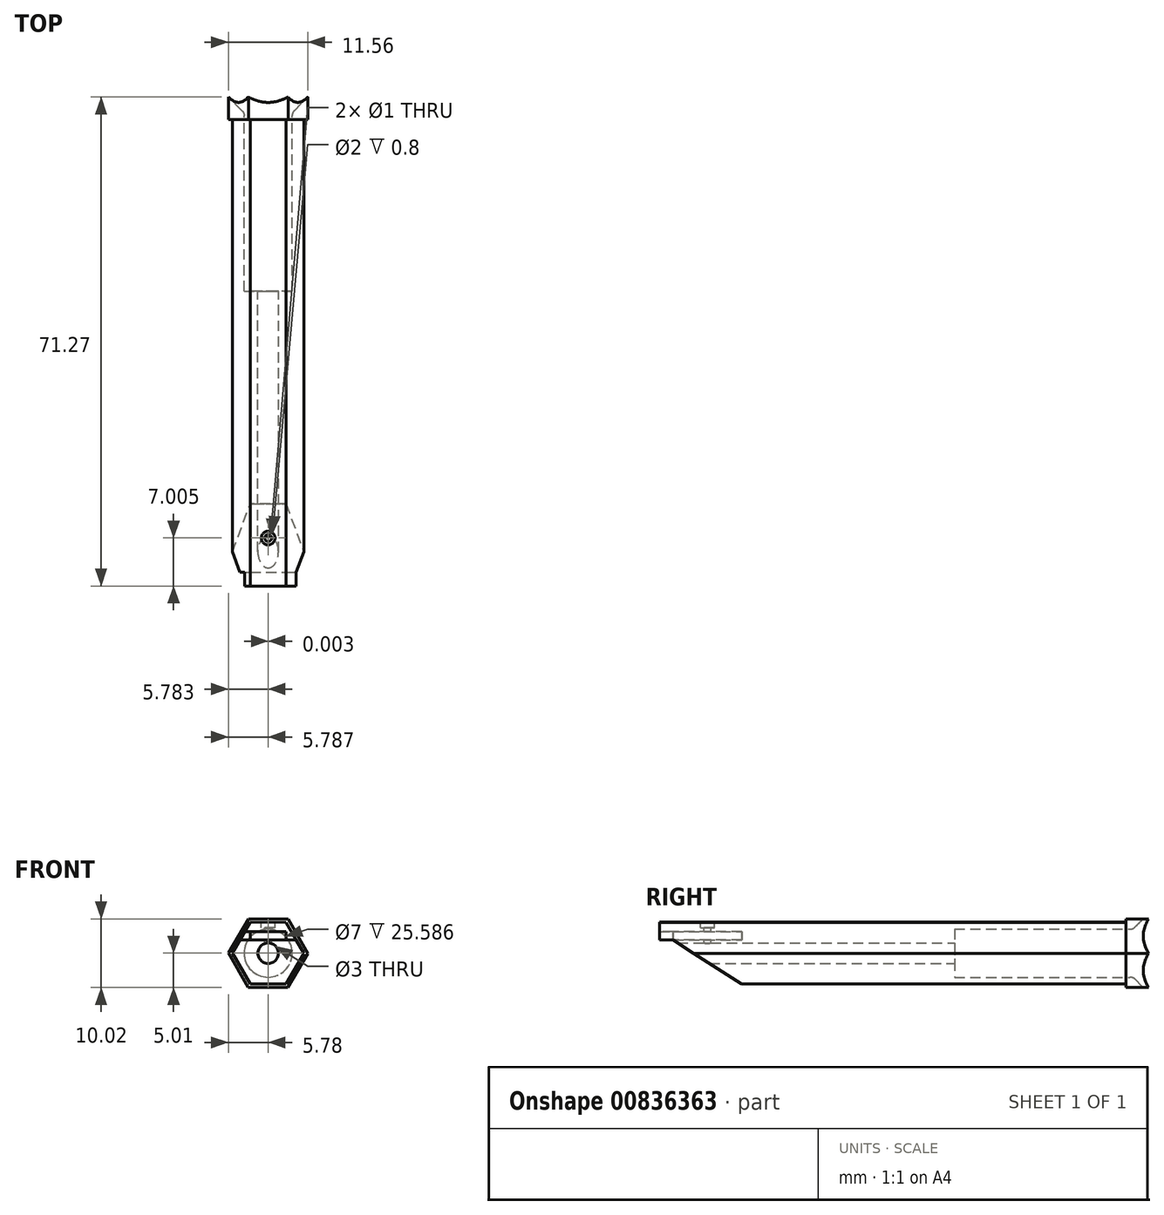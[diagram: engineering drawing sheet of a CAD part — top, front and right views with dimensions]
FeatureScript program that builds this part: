
annotation { "Feature Type Name" : "Feature", "Feature Type Description" : "" }
export const myFeature = defineFeature(function(context is Context, id is Id, definition is map)
    precondition{}
    {
        {
            var Q0;
            Q0=qCreatedBy(makeId("Front.planeOp"),FACE);
            var sketch = newSketch(context, id + "F0", { "sketchPlane" : qUnion([Q0])});
            skLineSegment(sketch, "E0.0", {"start": v(2.6, 4.5) * mm, "end": v(5.2, 0) * mm});
            skLineSegment(sketch, "E0.1", {"start": v(5.2, 0) * mm, "end": v(2.6, -4.5) * mm});
            skLineSegment(sketch, "E0.2", {"start": v(2.6, -4.5) * mm, "end": v(-2.6, -4.5) * mm});
            skLineSegment(sketch, "E0.3", {"start": v(-2.6, -4.5) * mm, "end": v(-5.2, 0) * mm});
            skLineSegment(sketch, "E0.4", {"start": v(-5.2, 0) * mm, "end": v(-2.6, 4.5) * mm});
            skLineSegment(sketch, "E0.5", {"start": v(-2.6, 4.5) * mm, "end": v(2.6, 4.5) * mm});
            skPoint(sketch, "E0.0.midPoint", {"position": v(3.9, 2.25) * mm});
            skSolve(sketch);
        }
        {
            var Q0;
            Q0=makeQuery(id+"F0.imprint","IMPRINT",FACE,{"disambiguationData":[TD([[makeQuery(id+"F0.imprint","IMPRINT",EDGE,{"derivedFrom":sQuery(id+"F0.wireOp",EDGE,"E0.0")}),-1.0]])]});
            extrude(context, id + "F1", {"entities" : qUnion([Q0]), "depth" : 70 * mm, "offsetDistance" : 25 * mm});
        }
        {
            var Q0;
            Q0=makeQuery(id+"F1.opExtrude","CAP_FACE",FACE,{"disambiguationData":[OSD([sQuery(id+"F0.wireOp",EDGE,"E0.0"),sQuery(id+"F0.wireOp",EDGE,"E0.1"),sQuery(id+"F0.wireOp",EDGE,"E0.2"),sQuery(id+"F0.wireOp",EDGE,"E0.3"),sQuery(id+"F0.wireOp",EDGE,"E0.4"),sQuery(id+"F0.wireOp",EDGE,"E0.5")])],"isStart":true});
            var sketch = newSketch(context, id + "F2", { "sketchPlane" : qUnion([Q0])});
            skLineSegment(sketch, "E1", {"start": v(2.6, 4.5) * mm, "end": v(5.2, 0) * mm});
            skLineSegment(sketch, "E2", {"start": v(5.2, 0) * mm, "end": v(3.9, 2.26) * mm});
            skSolve(sketch);
        }
        {
            var Q0;
            Q0=makeQuery(id+"F2.imprint","IMPRINT",FACE,{"disambiguationData":[TD([[makeQuery(id+"F2.imprint","IMPRINT",EDGE,{"derivedFrom":sQuery(id+"F2.wireOp",EDGE,"E1")}),1.0]])]});
            var sketch = newSketch(context, id + "F3", { "sketchPlane" : qUnion([Q0])});
            skLineSegment(sketch, "E3.1", {"start": v(5.86, 0.15) * mm, "end": v(2.73, -5.28) * mm});
            skLineSegment(sketch, "E3.5", {"start": v(-3.06, 5) * mm, "end": v(3.2, 5) * mm});
            skPoint(sketch, "E3.0.midPoint", {"position": v(4.74, 2.65) * mm});
            skLineSegment(sketch, "E4", {"start": v(-5.2, 0) * mm, "end": v(-2.6, -4.5) * mm});
            skLineSegment(sketch, "E5", {"start": v(-2.6, -4.5) * mm, "end": v(2.6, -4.5) * mm});
            skLineSegment(sketch, "E6", {"start": v(2.6, -4.5) * mm, "end": v(5.2, 0) * mm});
            skLineSegment(sketch, "E7", {"start": v(5.2, 0) * mm, "end": v(2.6, 4.5) * mm});
            skLineSegment(sketch, "E8", {"start": v(2.6, 4.5) * mm, "end": v(-2.6, 4.5) * mm});
            skLineSegment(sketch, "E9", {"start": v(-2.6, 4.5) * mm, "end": v(-5.2, 0) * mm});
            skLineSegment(sketch, "E10", {"start": v(2.16, 4.5) * mm, "end": v(2.16, 5) * mm});
            skLineSegment(sketch, "E11", {"start": v(-2.12, 4.5) * mm, "end": v(-2.12, 5) * mm});
            skLineSegment(sketch, "E12", {"start": v(-2.85, 4.07) * mm, "end": v(-3.29, 4.32) * mm});
            skLineSegment(sketch, "E13", {"start": v(-4.92, 0.48) * mm, "end": v(-5.35, 0.73) * mm});
            skLineSegment(sketch, "E14", {"start": v(-4.8, -0.7) * mm, "end": v(-5.24, -0.95) * mm});
            skLineSegment(sketch, "E15", {"start": v(-2.97, -3.86) * mm, "end": v(-3.4, -4.1) * mm});
            skLineSegment(sketch, "E16", {"start": v(-2.19, -4.5) * mm, "end": v(-2.19, -5) * mm});
            skLineSegment(sketch, "E17", {"start": v(2.17, -4.5) * mm, "end": v(2.17, -5) * mm});
            skLineSegment(sketch, "E18", {"start": v(2.9, -3.98) * mm, "end": v(3.34, -4.23) * mm});
            skLineSegment(sketch, "E19", {"start": v(4.97, -0.38) * mm, "end": v(5.4, -0.63) * mm});
            skLineSegment(sketch, "E20", {"start": v(4.86, 0.59) * mm, "end": v(5.3, 0.84) * mm});
            skLineSegment(sketch, "E21", {"start": v(2.88, 4.02) * mm, "end": v(3.3, 4.27) * mm});
            skLineSegment(sketch, "E22", {"start": v(3.3, 4.27) * mm, "end": v(5.78, 0) * mm});
            skLineSegment(sketch, "E23", {"start": v(3.3, 4.27) * mm, "end": v(2.88, 5) * mm});
            skLineSegment(sketch, "E24", {"start": v(-5.35, 0.73) * mm, "end": v(-2.9, 5) * mm});
            skLineSegment(sketch, "E25", {"start": v(-2.19, -5) * mm, "end": v(2.9, -5) * mm});
            skLineSegment(sketch, "E26", {"start": v(-2.19, -5) * mm, "end": v(-2.88, -5) * mm});
            skLineSegment(sketch, "E27", {"start": v(-5.24, -0.95) * mm, "end": v(-2.77, -5.2) * mm});
            skLineSegment(sketch, "E28", {"start": v(-3.29, 4.32) * mm, "end": v(-6.02, -0.44) * mm});
            skLineSegment(sketch, "E29", {"start": v(-5.24, -0.95) * mm, "end": v(-5.78, 0) * mm});
            skSolve(sketch);
        }
        {
            var Q0;
            Q0=makeQuery(id+"F2.imprint","IMPRINT",FACE,{"disambiguationData":[TD([[makeQuery(id+"F2.imprint","IMPRINT",EDGE,{"derivedFrom":sQuery(id+"F2.wireOp",EDGE,"E1")}),1.0]])]});
            var sketch = newSketch(context, id + "F4", { "sketchPlane" : qUnion([Q0])});
            skCircle(sketch, "E30", {"center": v(0, 0) * mm, "radius": 3.5 * mm});
            skSolve(sketch);
        }
        {
            var Q0;
            Q0=qSketchRegion(id+"F4",true);
            extrude(context, id + "F5", {"entities" : qUnion([Q0]), "operationType" : NewBodyOperationType.REMOVE, "oppositeDirection" : true, "depth" : 25 * mm, "offsetDistance" : 25 * mm});
        }
        {
            var Q0;
            Q0=makeQuery(id+"F1.opExtrude","SWEPT_FACE",FACE,{"disambiguationData":[OSD([sQuery(id+"F0.wireOp",EDGE,"E0.0")])]});
            var sketch = newSketch(context, id + "F6", { "sketchPlane" : qUnion([Q0])});
            skLineSegment(sketch, "E31", {"start": v(-70, 2.6) * mm, "end": v(-70, -2.6) * mm});
            skLineSegment(sketch, "E32", {"start": v(-70, -2.6) * mm, "end": v(-63, -2.6) * mm});
            skLineSegment(sketch, "E33", {"start": v(-63, -2.6) * mm, "end": v(-70, 2.6) * mm});
            skSolve(sketch);
        }
        {
            var Q0;
            Q0=makeQuery(id+"F1.opExtrude","SWEPT_FACE",FACE,{"disambiguationData":[OSD([sQuery(id+"F0.wireOp",EDGE,"E0.4")])]});
            var sketch = newSketch(context, id + "F7", { "sketchPlane" : qUnion([Q0])});
            skLineSegment(sketch, "E34", {"start": v(70, 2.6) * mm, "end": v(70, -2.6) * mm});
            skLineSegment(sketch, "E35", {"start": v(70, -2.6) * mm, "end": v(63, -2.6) * mm});
            skLineSegment(sketch, "E36", {"start": v(63, -2.6) * mm, "end": v(70, 2.6) * mm});
            skSolve(sketch);
        }
        {
            var Q0;
            Q0=qSketchRegion(id+"F6",true);
            extrude(context, id + "F8", {"entities" : qUnion([Q0]), "operationType" : NewBodyOperationType.REMOVE, "oppositeDirection" : true, "depth" : 25 * mm, "offsetDistance" : 25 * mm, "hasDraft" : true, "draftAngle" : 24.87 * degree});
        }
        {
            var Q0;
            Q0=makeQuery(id+"F7.imprint","IMPRINT",FACE,{"disambiguationData":[TD([[makeQuery(id+"F7.imprint","IMPRINT",EDGE,{"derivedFrom":sQuery(id+"F7.wireOp",EDGE,"E34")}),1.0]])]});
            extrude(context, id + "F9", {"entities" : qUnion([Q0]), "operationType" : NewBodyOperationType.REMOVE, "oppositeDirection" : true, "depth" : 25 * mm, "offsetDistance" : 25 * mm, "hasDraft" : true, "draftAngle" : 24.87 * degree});
        }
        {
            var Q0;
            Q0=makeQuery(id+"F1.opExtrude","SWEPT_FACE",FACE,{"disambiguationData":[OSD([sQuery(id+"F0.wireOp",EDGE,"E0.0")])]});
            var sketch = newSketch(context, id + "F10", { "sketchPlane" : qUnion([Q0])});
            skLineSegment(sketch, "E37", {"start": v(-68.6, 2.16) * mm, "end": v(-68.6, 2.6) * mm});
            skLineSegment(sketch, "E38", {"start": v(-65.98, 2.6) * mm, "end": v(-65.98, -0.38) * mm});
            skLineSegment(sketch, "E39", {"start": v(-65.98, -0.38) * mm, "end": v(-65.98, 1.1) * mm});
            skPoint(sketch, "E40", {"position": v(-65.98, 1.1) * mm});
            skLineSegment(sketch, "E41", {"start": v(-65.98, 2.6) * mm, "end": v(-70, 2.6) * mm});
            skSolve(sketch);
        }
        {
            var Q0;
            Q0=makeQuery(id+"F1.opExtrude","SWEPT_FACE",FACE,{"disambiguationData":[OSD([sQuery(id+"F0.wireOp",EDGE,"E0.4")])]});
            var sketch = newSketch(context, id + "F11", { "sketchPlane" : qUnion([Q0])});
            skLineSegment(sketch, "E42", {"start": v(70, 2.6) * mm, "end": v(65.99, 2.6) * mm});
            skLineSegment(sketch, "E43", {"start": v(65.99, 2.6) * mm, "end": v(65.99, -0.38) * mm});
            skLineSegment(sketch, "E44", {"start": v(65.99, -0.38) * mm, "end": v(70, 2.6) * mm});
            skLineSegment(sketch, "E45", {"start": v(65.99, 2.6) * mm, "end": v(65.99, 1.1) * mm});
            skPoint(sketch, "E46", {"position": v(65.99, 1.1) * mm});
            skSolve(sketch);
        }
        {
            var Q0;
            Q0=makeQuery(id+"F1.opExtrude","SWEPT_FACE",FACE,{"disambiguationData":[OSD([sQuery(id+"F0.wireOp",EDGE,"E0.5")])]});
            var sketch = newSketch(context, id + "F12", { "sketchPlane" : qUnion([Q0])});
            skLineSegment(sketch, "E47", {"start": v(-2.6, -70) * mm, "end": v(-2.6, -65.98) * mm});
            skLineSegment(sketch, "E48", {"start": v(-2.6, -65.98) * mm, "end": v(2.6, -65.98) * mm});
            skLineSegment(sketch, "E49", {"start": v(2.6, -65.98) * mm, "end": v(2.6, -70) * mm});
            skLineSegment(sketch, "E50", {"start": v(2.6, -70) * mm, "end": v(-2.6, -70) * mm});
            skSolve(sketch);
        }
        {
            var Q0;
            Q0=qSketchRegion(id+"F12",true);
            extrude(context, id + "F13", {"entities" : qUnion([Q0]), "operationType" : NewBodyOperationType.REMOVE, "oppositeDirection" : true, "depth" : 25 * mm, "offsetDistance" : 25 * mm});
        }
        {
            var Q0;
            Q0=makeQuery(id+"F11.imprint","IMPRINT",FACE,{"disambiguationData":[TD([[makeQuery(id+"F11.imprint","IMPRINT",EDGE,{"derivedFrom":sQuery(id+"F11.wireOp",EDGE,"E42")}),1.0]])]});
            extrude(context, id + "F14", {"entities" : qUnion([Q0]), "operationType" : NewBodyOperationType.REMOVE, "oppositeDirection" : true, "depth" : 25 * mm, "offsetDistance" : 25 * mm});
        }
        {
            var Q0;
            {var subQ4=sQuery(id+"F10.wireOp",EDGE,"E38");Q0=makeQuery(id+"F10.imprint","IMPRINT",FACE,{"disambiguationData":[TD([[makeQuery(id+"F10.imprint","IMPRINT",EDGE,{"derivedFrom":subQ4}),-1.0]])]});}
            extrude(context, id + "F15", {"entities" : qUnion([Q0]), "operationType" : NewBodyOperationType.REMOVE, "oppositeDirection" : true, "depth" : 25 * mm, "offsetDistance" : 25 * mm});
        }
        {
            var Q0;
            Q0=makeQuery(id+"F14.boolean.opBoolean","MERGE",FACE,{"derivedFrom":[makeQuery(id+"F13.boolean.opBoolean","COPY",FACE,{"derivedFrom":makeQuery(id+"F13.opExtrude","SWEPT_FACE",FACE,{"disambiguationData":[OSD([sQuery(id+"F12.wireOp",EDGE,"E48")])]})}),makeQuery(id+"F14.opExtrude","SWEPT_FACE",FACE,{"disambiguationData":[OSD([sQuery(id+"F11.wireOp",EDGE,"E43"),sQuery(id+"F11.wireOp",EDGE,"E45")])]})]});
            var sketch = newSketch(context, id + "F16", { "sketchPlane" : qUnion([Q0])});
            skLineSegment(sketch, "E51", {"start": v(-2.6, 4.5) * mm, "end": v(-2.6, 4.5) * mm});
            skLineSegment(sketch, "E52", {"start": v(-2.6, 4.5) * mm, "end": v(-2.6, 2.5) * mm});
            skLineSegment(sketch, "E53", {"start": v(2.6, 4.5) * mm, "end": v(2.6, 4.5) * mm});
            skLineSegment(sketch, "E54", {"start": v(2.6, 4.5) * mm, "end": v(2.2, -231.47) * mm});
            skLineSegment(sketch, "E55", {"start": v(-2.6, 2.5) * mm, "end": v(-2.6, 3.7) * mm});
            skLineSegment(sketch, "E56", {"start": v(2.2, -231.47) * mm, "end": v(2.4, -113.49) * mm});
            skLineSegment(sketch, "E57", {"start": v(2.2, -231.47) * mm, "end": v(3, 237.7) * mm});
            skLineSegment(sketch, "E58", {"start": v(-2.6, 2.5) * mm, "end": v(-2.6, 1.93) * mm});
            skLineSegment(sketch, "E59", {"start": v(2.2, 1.92) * mm, "end": v(2.2, -231.47) * mm});
            skLineSegment(sketch, "E60", {"start": v(2.2, 1.92) * mm, "end": v(-2.6, 1.93) * mm});
            skLineSegment(sketch, "E61", {"start": v(-2.6, 1.93) * mm, "end": v(-2.6, 3.13) * mm});
            skLineSegment(sketch, "E62", {"start": v(2.6, 3.12) * mm, "end": v(-2.6, 3.13) * mm});
            skLineSegment(sketch, "E63", {"start": v(2.6, 4.5) * mm, "end": v(2.6, 1.92) * mm});
            skLineSegment(sketch, "E64", {"start": v(2.6, 1.92) * mm, "end": v(2.6, 3.12) * mm});
            skSolve(sketch);
        }
        {
            var Q0;
            {var subQ1=sQuery(id+"F16.wireOp",EDGE,"E60");Q0=makeQuery(id+"F16.imprint","IMPRINT",FACE,{"disambiguationData":[TD([[makeQuery(id+"F16.imprint","IMPRINT",EDGE,{"derivedFrom":subQ1}),1.0]])]});}
            extrude(context, id + "F17", {"entities" : qUnion([Q0]), "operationType" : NewBodyOperationType.REMOVE, "oppositeDirection" : true, "depth" : 10 * mm, "offsetDistance" : 25 * mm});
        }
        {
            var Q0;
            Q0=makeQuery(id+"F1.opExtrude","SWEPT_FACE",FACE,{"disambiguationData":[OSD([sQuery(id+"F0.wireOp",EDGE,"E0.5")])]});
            var sketch = newSketch(context, id + "F18", { "sketchPlane" : qUnion([Q0])});
            skLineSegment(sketch, "E65", {"start": v(-2.6, -65.98) * mm, "end": v(2.6, -65.98) * mm});
            skLineSegment(sketch, "E66", {"start": v(2.6, -65.98) * mm, "end": v(2.6, -55.98) * mm});
            skLineSegment(sketch, "E67", {"start": v(2.6, -55.98) * mm, "end": v(-2.6, -55.98) * mm});
            skLineSegment(sketch, "E68", {"start": v(-2.6, -55.98) * mm, "end": v(-2.6, -65.98) * mm});
            skLineSegment(sketch, "E69", {"start": v(-2.6, -60.98) * mm, "end": v(2.6, -60.98) * mm});
            skLineSegment(sketch, "E70", {"start": v(2.6, -60.98) * mm, "end": v(0, -60.98) * mm});
            skLineSegment(sketch, "E71", {"start": v(0, -60.98) * mm, "end": v(0, -55.98) * mm});
            skLineSegment(sketch, "E72", {"start": v(0, -55.98) * mm, "end": v(0, -65.98) * mm});
            skPoint(sketch, "E73", {"position": v(0, -60.98) * mm});
            skSolve(sketch);
        }
        {
            var Q0;
            Q0=sQuery(id+"F18.wireOp",VERTEX,"E73");
            var Q1;
            Q1=makeQuery(id+"F1.opExtrude","SWEPT_BODY",BODY,{"disambiguationData":[OSD([sQuery(id+"F0.wireOp",EDGE,"E0.0"),sQuery(id+"F0.wireOp",EDGE,"E0.1"),sQuery(id+"F0.wireOp",EDGE,"E0.2"),sQuery(id+"F0.wireOp",EDGE,"E0.3"),sQuery(id+"F0.wireOp",EDGE,"E0.4"),sQuery(id+"F0.wireOp",EDGE,"E0.5")])]});
            hole(context, id + "F19", {"style" : HoleStyle.C_BORE, "endStyle" : HoleEndStyle.BLIND, "holeDiameter" : 1 * mm, "cBoreDiameter" : 2 * mm, "cBoreDepth" : .8 * mm, "majorDiameter" : 5 * mm, "holeDepth" : 2 * mm, "isTappedThrough" : true, "tappedDepth" : 12 * mm, "tapClearance" : 3, "startFromSketch" : true, "locations" : qUnion([Q0]), "scope" : qUnion([Q1])});
        }
        {
            var Q0;
            Q0=makeQuery(id+"F17.boolean.opBoolean","COPY",FACE,{"derivedFrom":makeQuery(id+"F17.opExtrude","SWEPT_FACE",FACE,{"disambiguationData":[OSD([sQuery(id+"F6.wireOp",EDGE,"E33"),sQuery(id+"F12.wireOp",EDGE,"E48"),sQuery(id+"F16.wireOp",EDGE,"E60")])]})});
            var sketch = newSketch(context, id + "F20", { "sketchPlane" : qUnion([Q0])});
            skLineSegment(sketch, "E74", {"start": v(-2.6, -65.99) * mm, "end": v(-2.6, -55.99) * mm});
            skLineSegment(sketch, "E75", {"start": v(-2.6, -55.99) * mm, "end": v(2.6, -55.98) * mm});
            skLineSegment(sketch, "E76", {"start": v(2.6, -55.98) * mm, "end": v(2.6, -65.98) * mm});
            skLineSegment(sketch, "E77", {"start": v(2.6, -65.98) * mm, "end": v(-2.6, -65.99) * mm});
            skLineSegment(sketch, "E78", {"start": v(0, -65.98) * mm, "end": v(0, -55.98) * mm});
            skLineSegment(sketch, "E79", {"start": v(2.6, -60.98) * mm, "end": v(-2.6, -60.99) * mm});
            skPoint(sketch, "E80", {"position": v(0, -60.98) * mm});
            skSolve(sketch);
        }
        {
            var Q0;
            Q0=sQuery(id+"F20.wireOp",VERTEX,"E80");
            var Q1;
            Q1=makeQuery(id+"F1.opExtrude","SWEPT_BODY",BODY,{"disambiguationData":[OSD([sQuery(id+"F0.wireOp",EDGE,"E0.0"),sQuery(id+"F0.wireOp",EDGE,"E0.1"),sQuery(id+"F0.wireOp",EDGE,"E0.2"),sQuery(id+"F0.wireOp",EDGE,"E0.3"),sQuery(id+"F0.wireOp",EDGE,"E0.4"),sQuery(id+"F0.wireOp",EDGE,"E0.5")])]});
            hole(context, id + "F21", {"style" : HoleStyle.SIMPLE, "endStyle" : HoleEndStyle.BLIND, "holeDiameter" : 1 * mm, "majorDiameter" : 5 * mm, "holeDepth" : 2 * mm, "isTappedThrough" : true, "tappedDepth" : 12 * mm, "tapClearance" : 3, "startFromSketch" : true, "locations" : qUnion([Q0]), "scope" : qUnion([Q1])});
        }
        {
            var Q0;
            Q0=makeQuery(id+"F5.boolean.opBoolean","COPY",FACE,{"derivedFrom":makeQuery(id+"F5.opExtrude","CAP_FACE",FACE,{"disambiguationData":[OSD([sQuery(id+"F4.wireOp",EDGE,"E30")])],"isStart":false})});
            var sketch = newSketch(context, id + "F22", { "sketchPlane" : qUnion([Q0])});
            skCircle(sketch, "E81", {"center": v(0, 0) * mm, "radius": 1.5 * mm});
            skSolve(sketch);
        }
        {
            var Q0;
            {var subQ2=makeQuery(id+"F2.imprint","IMPRINT",EDGE,{"derivedFrom":sQuery(id+"F2.wireOp",EDGE,"E1")});Q0=makeQuery(id+"F3.imprint","IMPRINT",FACE,{"disambiguationData":[TD([[makeQuery(id+"F3.imprint","IMPRINT",EDGE,{"derivedFrom":subQ2}),1.0]])]});}
            var sketch = newSketch(context, id + "F23", { "sketchPlane" : qUnion([Q0])});
            skCircle(sketch, "E82", {"center": v(0, 0) * mm, "radius": 3.5 * mm});
            skSolve(sketch);
        }
        {
            var Q0;
            Q0=makeQuery(id+"F23.imprint","IMPRINT",FACE,{"disambiguationData":[TD([[makeQuery(id+"F23.imprint","IMPRINT",EDGE,{"derivedFrom":sQuery(id+"F23.wireOp",EDGE,"E82")}),-1.0]])]});
            extrude(context, id + "F24", {"entities" : qUnion([Q0]), "operationType" : NewBodyOperationType.ADD, "depth" : 5 * mm, "offsetDistance" : 25 * mm});
        }
        {
            var Q0;
            Q0=qSketchRegion(id+"F3",true);
            extrude(context, id + "F25", {"entities" : qUnion([Q0]), "operationType" : NewBodyOperationType.ADD, "depth" : 5 * mm, "offsetDistance" : 25 * mm});
        }
        {
            var Q0;
            Q0=makeQuery(id+"F24.opExtrude","CAP_EDGE",EDGE,{"disambiguationData":[OSD([sQuery(id+"F23.wireOp",EDGE,"E82")])],"isStart":false});
            chamfer(context, id + "F26", {"entities" : qUnion([Q0]), "width" : 4 * mm, "tangentPropagation" : true});
        }
        {
            var Q0;
            {var subQ0=sQuery(id+"F23.wireOp",EDGE,"E82");Q0=makeQuery(id+"F26.opChamfer","BLEND_EDGE",EDGE,{"blendedFrom":[makeQuery(id+"F24.opExtrude","CAP_EDGE",EDGE,{"disambiguationData":[OSD([subQ0])],"isStart":false}),makeQuery(id+"F24.boolean.opBoolean","MERGE",FACE,{"derivedFrom":[makeQuery(id+"F5.boolean.opBoolean","COPY",FACE,{"derivedFrom":makeQuery(id+"F5.opExtrude","SWEPT_FACE",FACE,{"disambiguationData":[OSD([sQuery(id+"F4.wireOp",EDGE,"E30")])]})}),makeQuery(id+"F24.opExtrude","SWEPT_FACE",FACE,{"disambiguationData":[OSD([subQ0])]})]})],"blendedInto":[makeQuery(id+"F24.boolean.opBoolean","MERGE",FACE,{"derivedFrom":[makeQuery(id+"F5.boolean.opBoolean","COPY",FACE,{"derivedFrom":makeQuery(id+"F5.opExtrude","SWEPT_FACE",FACE,{"disambiguationData":[OSD([sQuery(id+"F4.wireOp",EDGE,"E30")])]})}),makeQuery(id+"F24.opExtrude","SWEPT_FACE",FACE,{"disambiguationData":[OSD([subQ0])]})]})]});}
            fillet(context, id + "F27", {"entities" : qUnion([Q0]), "radius" : 1 * mm, "tangentPropagation" : true, "allowEdgeOverflow" : false});
        }
        {
            var Q0;
            Q0=makeQuery(id+"F13.boolean.opBoolean","COPY",FACE,{"derivedFrom":makeQuery(id+"F13.opExtrude","SWEPT_FACE",FACE,{"disambiguationData":[OSD([sQuery(id+"F12.wireOp",EDGE,"E47")])]})});
            extrude(context, id + "F28", {"entities" : qUnion([Q0]), "operationType" : NewBodyOperationType.REMOVE, "oppositeDirection" : true, "depth" : 25 * mm, "offsetDistance" : 25 * mm});
        }
        {
            var Q0;
            {var subQ0=sQuery(id+"F12.wireOp",EDGE,"E48");Q0=makeQuery(id+"F28.boolean.opBoolean","MERGE",FACE,{"derivedFrom":[makeQuery(id+"F13.boolean.opBoolean","COPY",FACE,{"derivedFrom":makeQuery(id+"F13.opExtrude","SWEPT_FACE",FACE,{"disambiguationData":[OSD([subQ0])]})}),makeQuery(id+"F28.opExtrude","SWEPT_FACE",FACE,{"disambiguationData":[OSD([sQuery(id+"F0.wireOp",EDGE,"E0.4"),sQuery(id+"F0.wireOp",EDGE,"E0.5"),sQuery(id+"F12.wireOp",EDGE,"E47"),subQ0,sQuery(id+"F16.wireOp",EDGE,"E61")])]})]});}
            extrude(context, id + "F29", {"entities" : qUnion([Q0]), "operationType" : NewBodyOperationType.ADD, "depth" : 2 * mm, "offsetDistance" : 25 * mm});
        }
        {
            var Q0;
            Q0=makeQuery(id+"F15.boolean.opBoolean","COPY",FACE,{"derivedFrom":makeQuery(id+"F15.opExtrude","SWEPT_FACE",FACE,{"disambiguationData":[OSD([sQuery(id+"F10.wireOp",EDGE,"E38"),sQuery(id+"F10.wireOp",EDGE,"E39")])]})});
            extrude(context, id + "F30", {"entities" : qUnion([Q0]), "operationType" : NewBodyOperationType.ADD, "depth" : 2 * mm, "offsetDistance" : 25 * mm});
        }
        {
            var Q0;
            Q0=makeQuery(id+"F23.imprint","IMPRINT",FACE,{"disambiguationData":[TD([[makeQuery(id+"F23.imprint","IMPRINT",EDGE,{"derivedFrom":sQuery(id+"F23.wireOp",EDGE,"E82")}),1.0]])]});
            var sketch = newSketch(context, id + "F31", { "sketchPlane" : qUnion([Q0])});
            skCircle(sketch, "E83", {"center": v(0, 0) * mm, "radius": 1.5 * mm});
            skSolve(sketch);
        }
        {
            var Q0;
            Q0=qSketchRegion(id+"F31",true);
            extrude(context, id + "F32", {"entities" : qUnion([Q0]), "operationType" : NewBodyOperationType.REMOVE, "oppositeDirection" : true, "depth" : 65.97 * mm, "offsetDistance" : 25 * mm});
        }
    });
